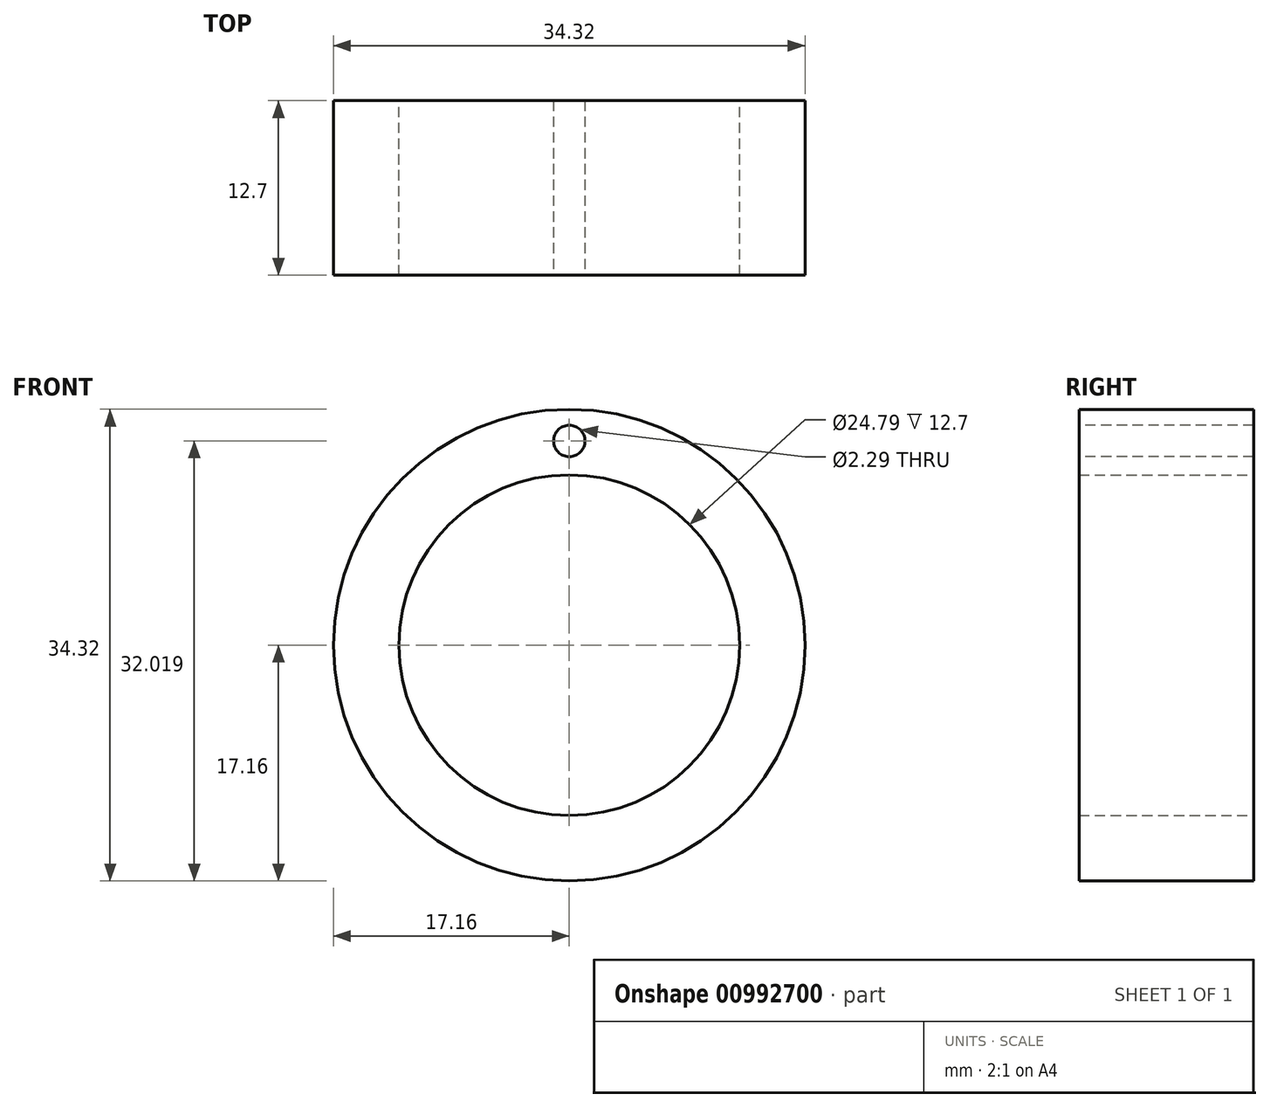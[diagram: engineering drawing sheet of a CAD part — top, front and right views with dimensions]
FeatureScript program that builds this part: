
annotation { "Feature Type Name" : "Feature", "Feature Type Description" : "" }
export const myFeature = defineFeature(function(context is Context, id is Id, definition is map)
    precondition{}
    {
        {
            var Q0;
            Q0=qCreatedBy(makeId("Top.planeOp"),FACE);
            var sketch = newSketch(context, id + "F0", { "sketchPlane" : qUnion([Q0])});
            skLineSegment(sketch, "E0", {"start": v(0, 4.38) * mm, "end": v(0, -7.47) * mm, "construction": true});
            skLineSegment(sketch, "E1", {"start": v(12.4, 6.35) * mm, "end": v(12.4, -6.35) * mm});
            skLineSegment(sketch, "E2", {"start": v(12.4, -6.35) * mm, "end": v(17.16, -6.35) * mm});
            skLineSegment(sketch, "E3", {"start": v(17.16, -6.35) * mm, "end": v(17.16, 6.35) * mm});
            skLineSegment(sketch, "E4", {"start": v(17.16, 6.35) * mm, "end": v(12.4, 6.35) * mm});
            skSolve(sketch);
        }
        {
            var Q0;
            Q0=qSketchRegion(id+"F0",true);
            var Q1;
            Q1=sQuery(id+"F0.wireOp",EDGE,"E0");
            revolve(context, id + "F1", {"surfaceOperationType" : NewSurfaceOperationType.NEW, "entities" : qUnion([Q0]), "axis" : qUnion([Q1]), "revolveType" : RevolveType.FULL});
        }
        {
            var Q0;
            Q0=qCreatedBy(makeId("Top.planeOp"),FACE);
            var sketch = newSketch(context, id + "F2", { "sketchPlane" : qUnion([Q0])});
            skLineSegment(sketch, "E5.left", {"start": v(1.27, 2.54) * mm, "end": v(1.27, -2.54) * mm});
            skLineSegment(sketch, "E5.right", {"start": v(-1.27, 2.54) * mm, "end": v(-1.27, -2.54) * mm});
            skPoint(sketch, "E5.middle", {"position": v(0, 0) * mm});
            skArc(sketch, "E6", {"start": v(-1.27, 2.54) * mm, "mid": v(0, 3.81) * mm, "end": v(1.27, 2.54) * mm});
            skArc(sketch, "E7", {"start": v(-1.27, -2.54) * mm, "mid": v(0, -3.81) * mm, "end": v(1.27, -2.54) * mm});
            skSolve(sketch);
        }
        {
            var Q0;
            Q0=makeQuery(id+"F1.opRevolve","SWEPT_FACE",FACE,{"disambiguationData":[OSD([sQuery(id+"F0.wireOp",EDGE,"E2")])]});
            var sketch = newSketch(context, id + "F3", { "sketchPlane" : qUnion([Q0])});
            skCircle(sketch, "E8", {"center": v(0, 0) * mm, "radius": 14.86 * mm, "construction": true});
            skCircle(sketch, "E9", {"center": v(0, 14.86) * mm, "radius": 1.14 * mm});
            skSolve(sketch);
        }
        {
            var Q0;
            Q0=qSketchRegion(id+"F3",true);
            extrude(context, id + "F4", {"entities" : qUnion([Q0]), "operationType" : NewBodyOperationType.REMOVE, "endBound" : BoundingType.UP_TO_NEXT, "oppositeDirection" : true, "depth" : 25.4 * mm, "offsetDistance" : 25.4 * mm});
        }
    });
